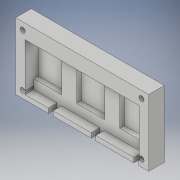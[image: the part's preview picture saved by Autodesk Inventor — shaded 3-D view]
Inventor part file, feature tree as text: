
AUTODESK INVENTOR PART (.ipt)
format: ipt  version: 2018 (Build 220112000, 112)  size: 179,200 bytes
history: native  units: in
note: dims shown in document units (in); Inventor stores cm internally (conversion verified against a paired STEP export)
features: extrude x4, sketch x3, hole x2, pattern_linear x1
ambient origin geometry x8: Origin, YZ Plane, XZ Plane, XY Plane, X Axis, Y Axis, Z Axis, Center Point
bodies: Solid1 (feature_tree)
feature tree (10):
  sketch  "Sketch1"  dims[d0=7.0in d1=3.5in]
  extrude  "Extrusion1"  Depth=3.5in
  extrude  "Extrusion2"  Depth=2.0in
  extrude  "Extrusion3"  Depth=0.5in
  extrude  "Extrusion4"  Depth=0.5in
  pattern_linear  "Rectangular Pattern1"  Spacing1=0.7in  [1 undecoded]
  hole  "Hole2"  [1 undecoded]
  sketch  "Sketch2"  dims[d2=1.475in d3=2.0in]
  sketch  "Sketch3"  dims[d4=0.5in d5=0.5in d6=0.5in d7=0.7in d8=0.0in d9=0.125in d10=0.0in d11=0.25in d12=0.0in d13=0.25in d14=0.25in d15=0.0in d16=1.1811in d18=2.25in d19=0.266in d20=0.75in d21=0.375in d22=0.25in d23=0.5635in d24=1.0in d25=0.0in]
  hole  "Hole1"  [1 undecoded]
note: 3 required parameter values undecoded (feature->parameter linkage not recoverable at this tier; creation-order binding heuristic only, values carry confidence <= 0.55)
